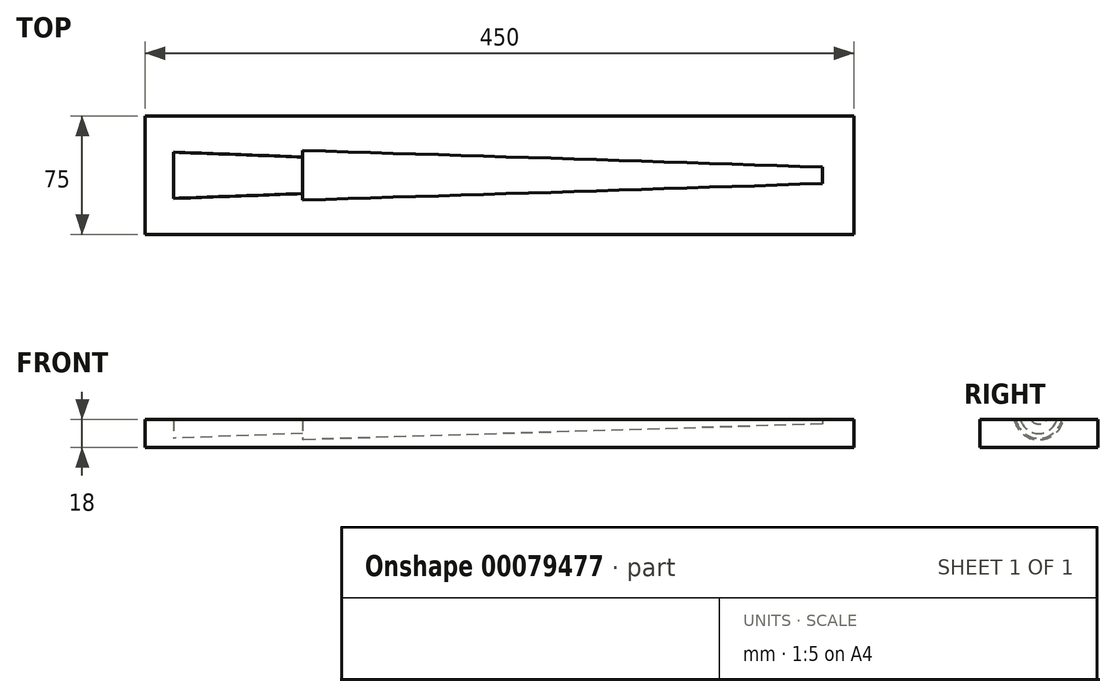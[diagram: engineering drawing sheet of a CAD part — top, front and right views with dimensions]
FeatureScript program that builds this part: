
annotation { "Feature Type Name" : "Feature", "Feature Type Description" : "" }
export const myFeature = defineFeature(function(context is Context, id is Id, definition is map)
    precondition{}
    {
        {
            var Q0;
            Q0=qCreatedBy(makeId("Top.planeOp"),FACE);
            var sketch = newSketch(context, id + "F0", { "sketchPlane" : qUnion([Q0])});
            skLineSegment(sketch, "E0.bottom", {"start": v(-271.44, 19.58) * mm, "end": v(178.56, 19.58) * mm});
            skLineSegment(sketch, "E0.top", {"start": v(-271.44, -55.42) * mm, "end": v(178.56, -55.42) * mm});
            skLineSegment(sketch, "E0.left", {"start": v(-271.44, 19.58) * mm, "end": v(-271.44, -55.42) * mm});
            skLineSegment(sketch, "E0.right", {"start": v(178.56, 19.58) * mm, "end": v(178.56, -55.42) * mm});
            skLineSegment(sketch, "E1", {"start": v(-282.34, -17.92) * mm, "end": v(306.49, -17.92) * mm, "construction": true});
            skLineSegment(sketch, "E2", {"start": v(-253.44, -17.92) * mm, "end": v(-253.44, -32.92) * mm});
            skLineSegment(sketch, "E3", {"start": v(-253.44, -32.92) * mm, "end": v(-171.44, -29.92) * mm});
            skLineSegment(sketch, "E4", {"start": v(-171.44, -29.92) * mm, "end": v(-171.44, -33.92) * mm});
            skLineSegment(sketch, "E5", {"start": v(-171.44, -33.92) * mm, "end": v(158.56, -23.92) * mm});
            skLineSegment(sketch, "E6", {"start": v(158.56, -23.92) * mm, "end": v(158.56, -17.92) * mm});
            skLineSegment(sketch, "E7", {"start": v(-253.44, -17.92) * mm, "end": v(158.56, -17.92) * mm});
            skSolve(sketch);
        }
        {
            var Q0;
            Q0=makeQuery(id+"F0.imprint","IMPRINT",FACE,{"disambiguationData":[TD([[makeQuery(id+"F0.imprint","IMPRINT",EDGE,{"derivedFrom":sQuery(id+"F0.wireOp",EDGE,"E0.bottom")}),-1.0]])]});
            var Q1;
            Q1=makeQuery(id+"F0.imprint","IMPRINT",FACE,{"disambiguationData":[TD([[makeQuery(id+"F0.imprint","IMPRINT",EDGE,{"derivedFrom":sQuery(id+"F0.wireOp",EDGE,"E2")}),1.0]])]});
            extrude(context, id + "F1", {"entities" : qUnion([Q0, Q1]), "oppositeDirection" : true, "depth" : 21 * mm, "hasSecondDirection" : true, "secondDirectionOppositeDirection" : true, "secondDirectionDepth" : 3 * mm});
        }
        {
            var Q0;
            Q0=makeQuery(id+"F0.imprint","IMPRINT",FACE,{"disambiguationData":[TD([[makeQuery(id+"F0.imprint","IMPRINT",EDGE,{"derivedFrom":sQuery(id+"F0.wireOp",EDGE,"E2")}),1.0]])]});
            var Q1;
            Q1=sQuery(id+"F0.wireOp",EDGE,"E1");
            revolve(context, id + "F2", {"operationType" : NewBodyOperationType.REMOVE, "entities" : qUnion([Q0]), "axis" : qUnion([Q1]), "revolveType" : RevolveType.FULL, "oppositeDirection" : true});
        }
    });
